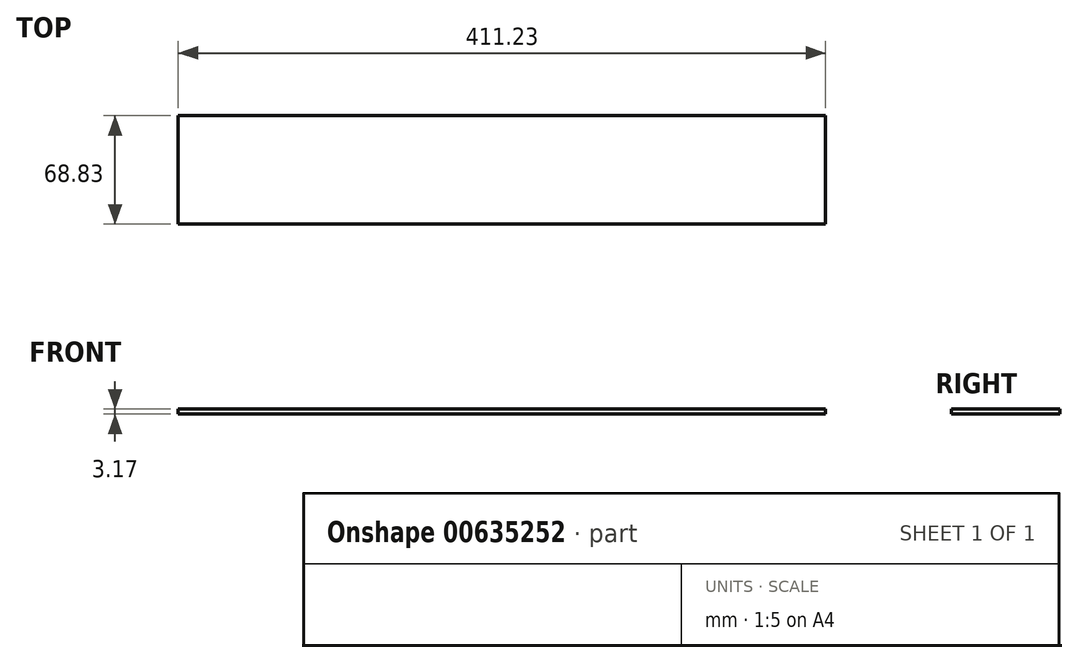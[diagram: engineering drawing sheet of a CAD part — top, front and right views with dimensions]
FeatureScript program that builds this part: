
annotation { "Feature Type Name" : "Feature", "Feature Type Description" : "" }
export const myFeature = defineFeature(function(context is Context, id is Id, definition is map)
    precondition{}
    {
        {
            var Q0;
            Q0=qCreatedBy(makeId("Top.planeOp"),FACE);
            var sketch = newSketch(context, id + "F0", { "sketchPlane" : qUnion([Q0])});
            skLineSegment(sketch, "E0.bottom", {"start": v(0, 0) * mm, "end": v(-411.23, 0) * mm});
            skLineSegment(sketch, "E0.top", {"start": v(0, 68.83) * mm, "end": v(-411.23, 68.83) * mm});
            skLineSegment(sketch, "E0.left", {"start": v(0, 0) * mm, "end": v(0, 68.83) * mm});
            skLineSegment(sketch, "E1", {"start": v(-431.8, 0) * mm, "end": v(-411.23, 68.83) * mm});
            skLineSegment(sketch, "E2", {"start": v(-411.23, 68.83) * mm, "end": v(-411.23, 0) * mm});
            skSolve(sketch);
        }
        {
            var Q0;
            Q0 = qSketchRegion(id + "F0", true);
            extrude(context, id + "F1", {"entities" : qUnion([Q0]), "depth" : 3.17 * mm, "offsetDistance" : 25.4 * mm});
        }
    });
